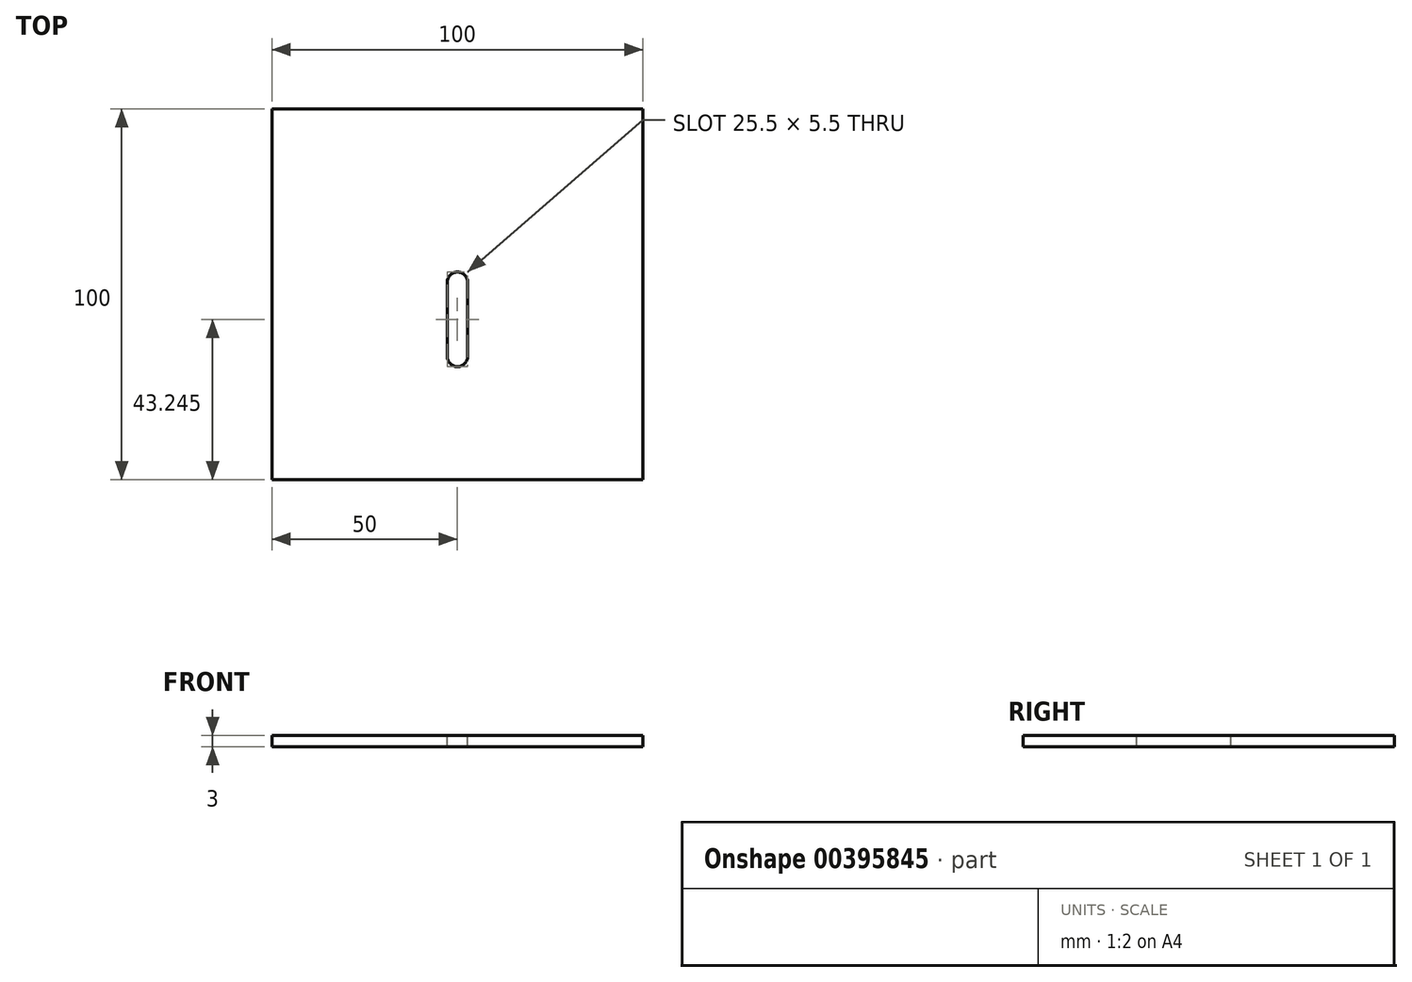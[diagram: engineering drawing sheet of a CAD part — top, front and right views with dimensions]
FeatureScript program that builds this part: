
annotation { "Feature Type Name" : "Feature", "Feature Type Description" : "" }
export const myFeature = defineFeature(function(context is Context, id is Id, definition is map)
    precondition{}
    {
        {
            var Q0;
            Q0=qCreatedBy(makeId("Top.planeOp"),FACE);
            var sketch = newSketch(context, id + "F0", { "sketchPlane" : qUnion([Q0])});
            skLineSegment(sketch, "E0.bottom", {"start": v(0, -50) * mm, "end": v(100, -50) * mm});
            skLineSegment(sketch, "E0.top", {"start": v(0, 50) * mm, "end": v(100, 50) * mm});
            skLineSegment(sketch, "E0.left", {"start": v(0, -50) * mm, "end": v(0, 50) * mm});
            skLineSegment(sketch, "E0.right", {"start": v(100, -50) * mm, "end": v(100, 50) * mm});
            skSolve(sketch);
        }
        {
            var Q0;
            Q0=makeQuery(id+"F0.imprint","IMPRINT",FACE,{"disambiguationData":[TD([[makeQuery(id+"F0.imprint","IMPRINT",EDGE,{"derivedFrom":sQuery(id+"F0.wireOp",EDGE,"E0.bottom")}),1.0]])]});
            extrude(context, id + "F1", {"entities" : qUnion([Q0]), "depth" : 3 * mm});
        }
        {
            var Q0;
            Q0=makeQuery(id+"F1.opExtrude","CAP_FACE",FACE,{"disambiguationData":[OSD([sQuery(id+"F0.wireOp",EDGE,"E0.bottom"),sQuery(id+"F0.wireOp",EDGE,"E0.top"),sQuery(id+"F0.wireOp",EDGE,"E0.left"),sQuery(id+"F0.wireOp",EDGE,"E0.right")])],"isStart":false});
            var sketch = newSketch(context, id + "F2", { "sketchPlane" : qUnion([Q0])});
            skLineSegment(sketch, "E1", {"start": v(50, 3.24) * mm, "end": v(50, -16.76) * mm});
            skArc(sketch, "E2.0.startCap", {"start": v(47.25, 3.24) * mm, "mid": v(50, 6) * mm, "end": v(52.75, 3.24) * mm});
            skArc(sketch, "E2.0.endCap", {"start": v(52.75, -16.76) * mm, "mid": v(50, -19.5) * mm, "end": v(47.25, -16.76) * mm});
            skLineSegment(sketch, "E2.0.left", {"start": v(52.75, 3.24) * mm, "end": v(52.75, -16.76) * mm});
            skLineSegment(sketch, "E2.0.right", {"start": v(47.25, 3.24) * mm, "end": v(47.25, -16.76) * mm});
            skSolve(sketch);
        }
        {
            var Q0;
            Q0=makeQuery(id+"F2.imprint","IMPRINT",FACE,{"disambiguationData":[TD([[makeQuery(id+"F2.imprint","IMPRINT",EDGE,{"derivedFrom":sQuery(id+"F2.wireOp",EDGE,"E2.0.startCap")}),1.0]])]});
            var Q1;
            Q1=sQuery(id+"F2.wireOp",EDGE,"E2.0.left");
            var Q2;
            Q2=sQuery(id+"F2.wireOp",EDGE,"E2.0.startCap");
            var Q3;
            Q3=sQuery(id+"F2.wireOp",EDGE,"E2.0.right");
            var Q4;
            Q4=sQuery(id+"F2.wireOp",EDGE,"E2.0.endCap");
            extrude(context, id + "F3", {"entities" : qUnion([Q0]), "operationType" : NewBodyOperationType.REMOVE, "surfaceEntities" : qUnion([Q1, Q2, Q3, Q4]), "endBound" : BoundingType.THROUGH_ALL, "oppositeDirection" : true, "depth" : 25.4 * mm});
        }
    });
